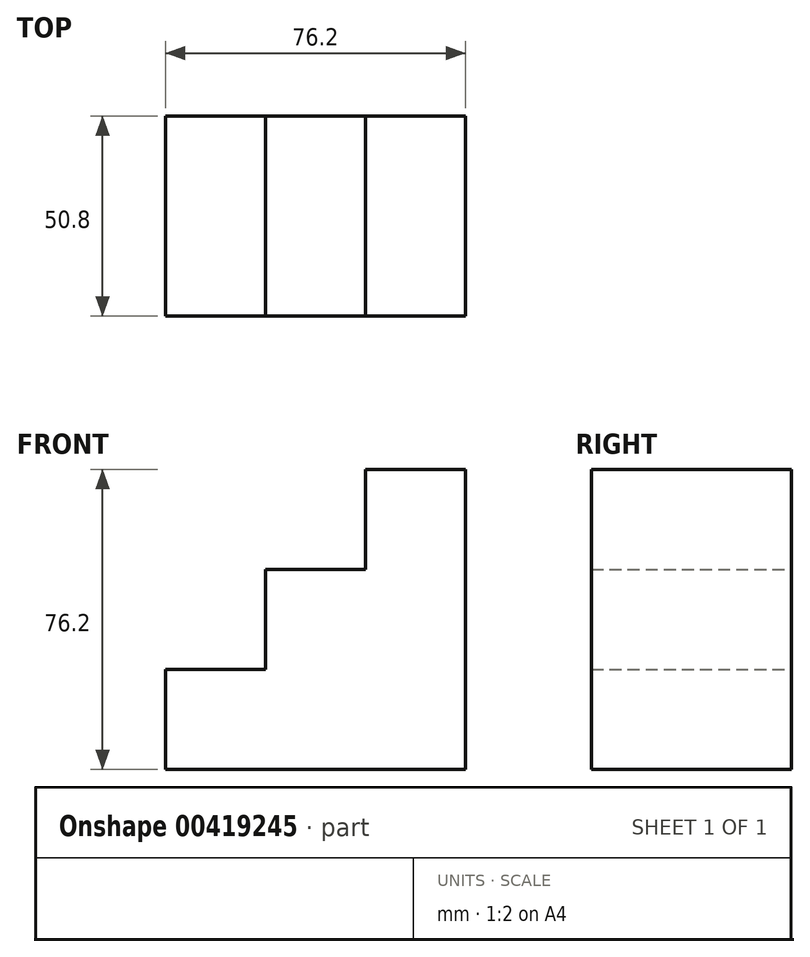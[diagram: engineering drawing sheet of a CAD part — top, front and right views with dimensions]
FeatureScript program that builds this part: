
annotation { "Feature Type Name" : "Feature", "Feature Type Description" : "" }
export const myFeature = defineFeature(function(context is Context, id is Id, definition is map)
    precondition{}
    {
        {
            var Q0;
            Q0=qCreatedBy(makeId("Front.planeOp"),FACE);
            var sketch = newSketch(context, id + "F0", { "sketchPlane" : qUnion([Q0])});
            skLineSegment(sketch, "E0", {"start": v(0, 0) * mm, "end": v(0, 25.4) * mm});
            skLineSegment(sketch, "E1", {"start": v(0, 25.4) * mm, "end": v(25.4, 25.4) * mm});
            skLineSegment(sketch, "E2", {"start": v(25.4, 25.4) * mm, "end": v(25.4, 50.8) * mm});
            skLineSegment(sketch, "E3", {"start": v(25.4, 50.8) * mm, "end": v(50.8, 50.8) * mm});
            skLineSegment(sketch, "E4", {"start": v(50.8, 50.8) * mm, "end": v(50.8, 76.2) * mm});
            skLineSegment(sketch, "E5", {"start": v(50.8, 76.2) * mm, "end": v(76.2, 76.2) * mm});
            skLineSegment(sketch, "E6", {"start": v(76.2, 76.2) * mm, "end": v(76.2, 0) * mm});
            skLineSegment(sketch, "E7", {"start": v(76.2, 0) * mm, "end": v(0, 0) * mm});
            skSolve(sketch);
        }
        {
            var Q0;
            Q0 = qSketchRegion(id + "F0", true);
            extrude(context, id + "F1", {"entities" : qUnion([Q0]), "depth" : 50.8 * mm});
        }
    });
